# Revit family: LIXIL - CC-PLATE-RND - COBRA CISTERN ACTUATOR PLATE
name_source: partatom
category: Plumbing Fixtures
units: mm (PartAtom-declared; Revit-internal decimal feet)

## family parameters
Always vertical = Yes
Cut with Voids When Loaded = No
Enable Cutting in Views = No
Maintain Annotation Orientation = No
OmniClass Number = 23.45.00.00
OmniClass Title = Sanitary, Laundry, and Cleaning Equipment
Part Type = Normal
Room Calculation Point = No
Round Connector Dimension = Use Diameter
Shared = Yes
Work Plane-Based = No

## types (1)
- CC-PLATE-RND
    Default Elevation = 0 mm  [stored 0 ft]
    Description = Cobra Cistern Actuator plate to detail and spec. See sanware schedule. Available from Lixil.
    Hosted on lixil.co.za = https://www.lixil.co.za
    M _ ACTUATOR PLATE _ BODY = M _ LIXIL - CHROME _ SATIN 02
    M _ ACTUATOR PLATE _ BUTTON 01 = M _ LIXIL - CHROME _ SATIN 02
    Product Specification = Supplier: Lixil.
Product description: Mechanical dual flush plate compatible with concealed cistern CC-CISTERN/N and CC-CISTERN/WH. 
Product Code: FCP2RD00-0GT01
SKU Code: CC-PLATE-RND
Barcode: 6002194055754
Brand: Cobra
Range: Cobra
Category: Toilets
Sub-Category: Actuator Plates
Colour: Chrome
Package Height: 50 mm
Package Width: 170 mm
Package Length: 250 mm
Package Volume: 2125000 mm³

Notes:
- Refer to manufacturer's and supplier's installation, maintenance and cleaning manual.
- Refer to manufacturer's and supplier's guarantees and warrantees document.

note: [stored X ft] marks values corroborated as IEEE doubles in the binary element streams (Revit-internal decimal feet)

## geometry (parser evidence)
native form markers: Sweep x6
no freeform markers — native parametric forms only
